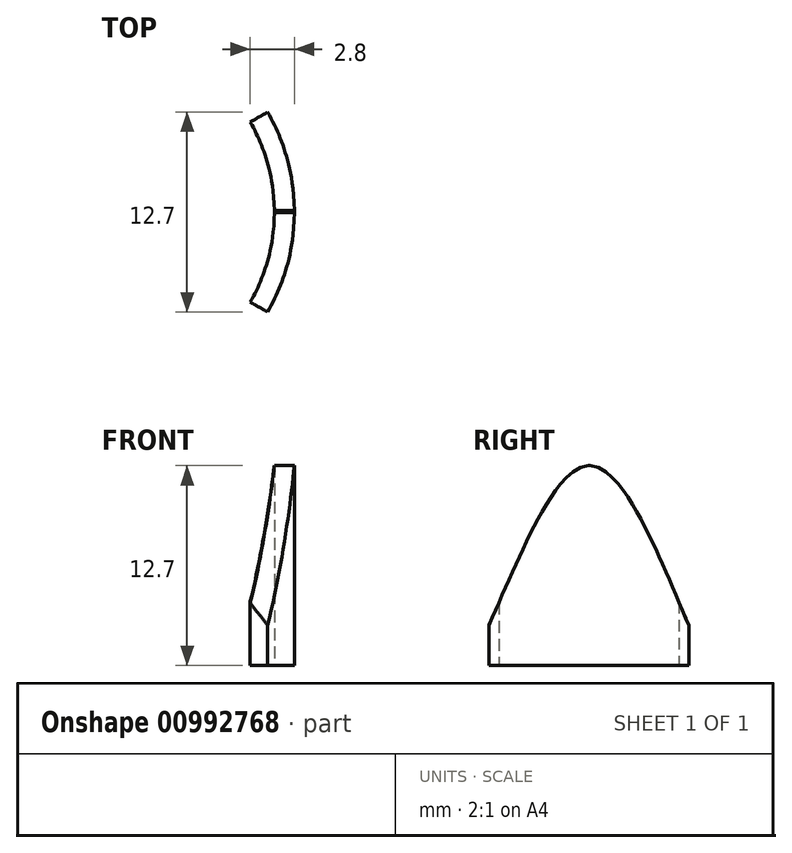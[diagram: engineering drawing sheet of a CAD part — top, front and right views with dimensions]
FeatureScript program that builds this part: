
annotation { "Feature Type Name" : "Feature", "Feature Type Description" : "" }
export const myFeature = defineFeature(function(context is Context, id is Id, definition is map)
    precondition{}
    {
        {
            var Q0;
            Q0=qCreatedBy(makeId("Top.planeOp"),FACE);
            var sketch = newSketch(context, id + "F0", { "sketchPlane" : qUnion([Q0])});
            skArc(sketch, "E0", {"start": v(0, -12.7) * mm, "mid": v(1.7, -6.35) * mm, "end": v(0, 0) * mm});
            skLineSegment(sketch, "E1.0", {"start": v(-0.84, -6.35) * mm, "end": v(-0.84, -6.35) * mm});
            skArc(sketch, "E2.0", {"start": v(-1.1, -12.07) * mm, "mid": v(0.43, -6.35) * mm, "end": v(-1.1, -0.63) * mm});
            skLineSegment(sketch, "E3", {"start": v(-1.1, -0.63) * mm, "end": v(0, 0) * mm});
            skLineSegment(sketch, "E4", {"start": v(-1.1, -12.07) * mm, "end": v(0, -12.7) * mm});
            skSolve(sketch);
        }
        {
            var Q0;
            Q0=makeQuery(id+"F0.imprint","IMPRINT",FACE,{"disambiguationData":[TD([[makeQuery(id+"F0.imprint","IMPRINT",EDGE,{"derivedFrom":sQuery(id+"F0.wireOp",EDGE,"E0")}),1.0]])]});
            var Q1;
            Q1 = qSketchRegion(id + "F2", true);
            extrude(context, id + "F1", {"entities" : qUnion([Q0, Q1]), "depth" : 12.7 * mm, "offsetDistance" : 25.4 * mm});
        }
        {
            var Q0;
            Q0=qCreatedBy(makeId("Right.planeOp"),FACE);
            var sketch = newSketch(context, id + "F2", { "sketchPlane" : qUnion([Q0])});
            skFitSpline(sketch, "E5", {"points": [v(0, 2.54) * mm, v(-6.37, 12.7) * mm, v(-12.7, 2.54) * mm], "startDerivative": vector(-12.71, 30.48) * mm, "endDerivative": vector(-12.61, -28.43) * mm});
            skLineSegment(sketch, "E6", {"start": v(0, 2.54) * mm, "end": v(0, 12.7) * mm});
            skLineSegment(sketch, "E7", {"start": v(0, 12.7) * mm, "end": v(-6.37, 12.7) * mm});
            skLineSegment(sketch, "E8", {"start": v(-6.37, 12.7) * mm, "end": v(-12.7, 12.7) * mm});
            skLineSegment(sketch, "E9", {"start": v(-12.7, 12.7) * mm, "end": v(-12.7, 2.54) * mm});
            skSolve(sketch);
        }
        {
            var Q0;
            Q0 = qSketchRegion(id + "F2", true);
            extrude(context, id + "F3", {"entities" : qUnion([Q0]), "operationType" : NewBodyOperationType.REMOVE, "endBound" : BoundingType.SYMMETRIC, "depth" : 12.7 * mm, "offsetDistance" : 25.4 * mm});
        }
    });
